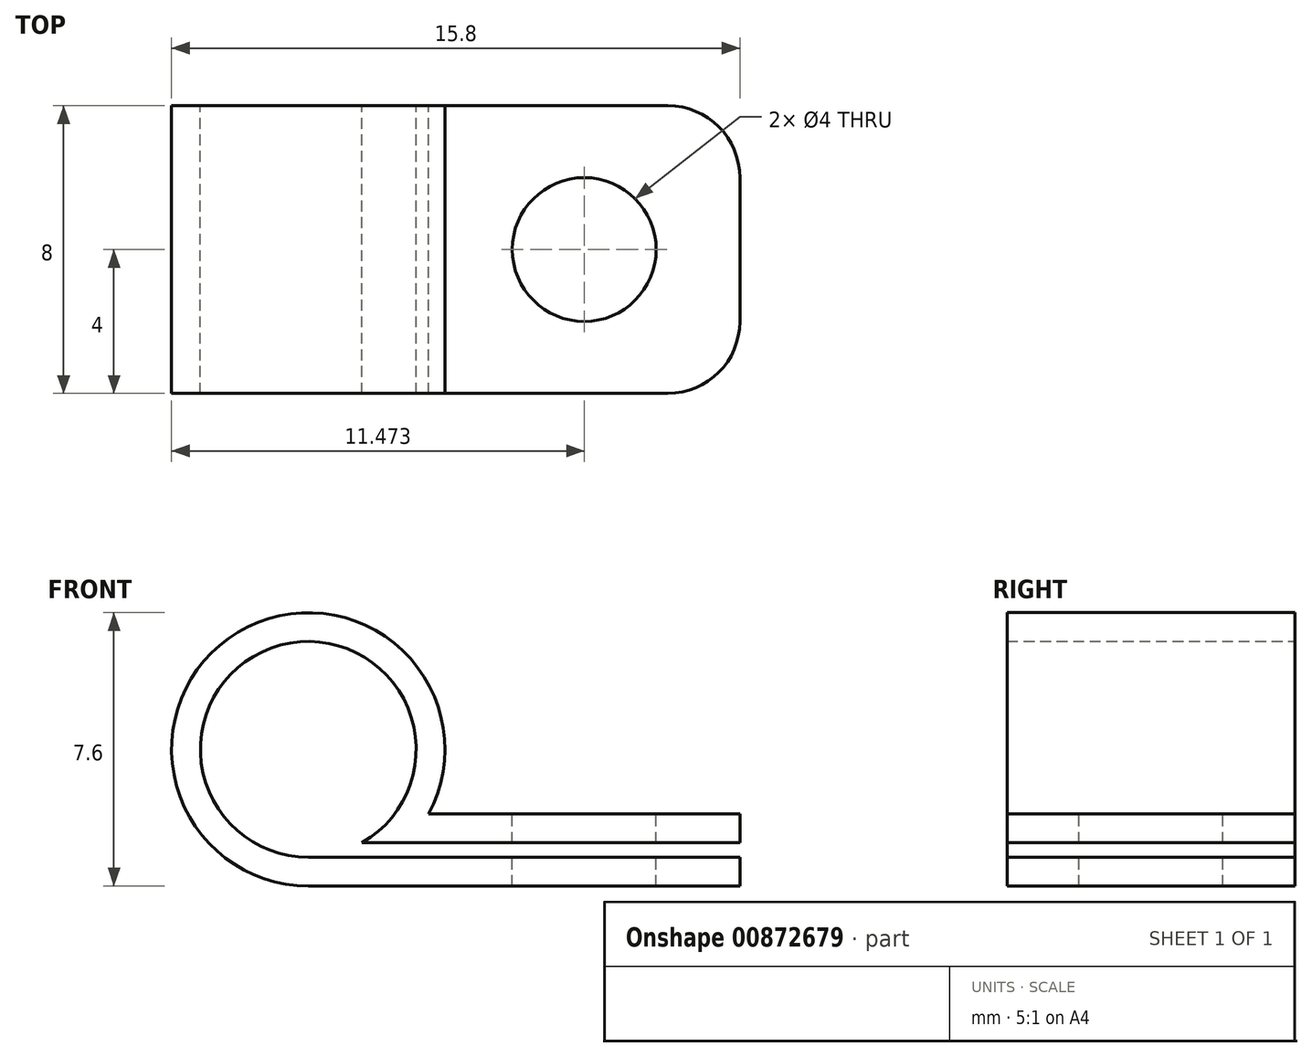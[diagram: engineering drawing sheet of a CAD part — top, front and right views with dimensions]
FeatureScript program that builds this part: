
annotation { "Feature Type Name" : "Feature", "Feature Type Description" : "" }
export const myFeature = defineFeature(function(context is Context, id is Id, definition is map)
    precondition{}
    {
        {
            var Q0;
            Q0=qCreatedBy(makeId("Front.planeOp"),FACE);
            var sketch = newSketch(context, id + "F0", { "sketchPlane" : qUnion([Q0])});
            skCircle(sketch, "E0", {"center": v(0, 0) * mm, "radius": 3 * mm});
            skCircle(sketch, "E1", {"center": v(0, 0) * mm, "radius": 3.8 * mm});
            skLineSegment(sketch, "E2.bottom", {"start": v(0, -3.8) * mm, "end": v(12, -3.8) * mm});
            skLineSegment(sketch, "E2.top", {"start": v(0, -3) * mm, "end": v(12, -3) * mm});
            skLineSegment(sketch, "E2.left", {"start": v(0, -3.8) * mm, "end": v(0, -3) * mm});
            skLineSegment(sketch, "E2.right", {"start": v(12, -3.8) * mm, "end": v(12, -3) * mm});
            skLineSegment(sketch, "E3", {"start": v(12, -3) * mm, "end": v(12, -2.6) * mm});
            skLineSegment(sketch, "E4.bottom", {"start": v(12, -2.6) * mm, "end": v(1.37, -2.6) * mm});
            skLineSegment(sketch, "E4.top", {"start": v(12, -1.8) * mm, "end": v(1.37, -1.8) * mm});
            skLineSegment(sketch, "E4.left", {"start": v(12, -2.6) * mm, "end": v(12, -1.8) * mm});
            skLineSegment(sketch, "E4.right", {"start": v(1.37, -2.6) * mm, "end": v(1.37, -1.8) * mm});
            skSolve(sketch);
        }
        {
            var Q0;
            {var subQ0=sQuery(id+"F0.wireOp",EDGE,"E2.left");Q0=makeQuery(id+"F0.imprint","IMPRINT",FACE,{"disambiguationData":[TD([[makeQuery(id+"F0.imprint","IMPRINT",EDGE,{"derivedFrom":subQ0}),1.0]])]});}
            var Q1;
            {var subQ0=sQuery(id+"F0.wireOp",EDGE,"l8cNaRmP-a3Ar-Ibxh-vkPG-nLSyhId6ISBD.bottom");var subQ1=sQuery(id+"F0.wireOp",EDGE,"E0");var subQ2=makeQuery(id+"F0.imprint","INTERSECT",VERTEX,{"derivedFrom":[subQ1,subQ0]});Q1=makeQuery(id+"F0.imprint","IMPRINT",FACE,{"disambiguationData":[TD([[makeQuery(id+"F0.imprint","IMPRINT",EDGE,{"disambiguationData":[TD([[subQ2,-1.0]])],"derivedFrom":subQ1}),-1.0]])]});}
            var Q2;
            {var subQ5=sQuery(id+"F0.wireOp",EDGE,"l8cNaRmP-a3Ar-Ibxh-vkPG-nLSyhId6ISBD.left");Q2=makeQuery(id+"F0.imprint","IMPRINT",FACE,{"disambiguationData":[TD([[makeQuery(id+"F0.imprint","IMPRINT",EDGE,{"derivedFrom":subQ5}),1.0]])]});}
            var Q3;
            {var subQ0=sQuery(id+"F0.wireOp",EDGE,"E2.bottom");Q3=makeQuery(id+"F0.imprint","IMPRINT",FACE,{"disambiguationData":[TD([[makeQuery(id+"F0.imprint","IMPRINT",EDGE,{"derivedFrom":subQ0}),1.0]])]});}
            var Q4;
            {var subQ0=sQuery(id+"F0.wireOp",EDGE,"E2.left");Q4=makeQuery(id+"F0.imprint","IMPRINT",FACE,{"disambiguationData":[TD([[makeQuery(id+"F0.imprint","IMPRINT",EDGE,{"derivedFrom":subQ0}),-1.0]])]});}
            var Q5;
            {var subQ0=sQuery(id+"F0.wireOp",EDGE,"E4.right");var subQ7=sQuery(id+"F0.wireOp",EDGE,"E0");var subQ9=makeQuery(id+"F0.imprint","INTERSECT",VERTEX,{"derivedFrom":[subQ7,subQ0]});Q5=makeQuery(id+"F0.imprint","IMPRINT",FACE,{"disambiguationData":[TD([[makeQuery(id+"F0.imprint","IMPRINT",EDGE,{"disambiguationData":[TD([[subQ9,-1.0]])],"derivedFrom":subQ7}),-1.0]])]});}
            var Q6;
            {var subQ5=sQuery(id+"F0.wireOp",EDGE,"E4.left");Q6=makeQuery(id+"F0.imprint","IMPRINT",FACE,{"disambiguationData":[TD([[makeQuery(id+"F0.imprint","IMPRINT",EDGE,{"derivedFrom":subQ5}),1.0]])]});}
            extrude(context, id + "F1", {"entities" : qUnion([Q0, Q1, Q2, Q3, Q4, Q5, Q6]), "depth" : 8 * mm, "offsetDistance" : 25 * mm});
        }
        {
            var Q0;
            Q0=makeQuery(id+"F1.opExtrude","SWEPT_FACE",FACE,{"disambiguationData":[OSD([sQuery(id+"F0.wireOp",EDGE,"E4.top")])]});
            var sketch = newSketch(context, id + "F2", { "sketchPlane" : qUnion([Q0])});
            skLineSegment(sketch, "E5", {"start": v(12, -4) * mm, "end": v(3.3, -4) * mm, "construction": true});
            skLineSegment(sketch, "E6", {"start": v(7.67, 0) * mm, "end": v(7.67, -8) * mm, "construction": true});
            skCircle(sketch, "E7", {"center": v(7.67, -4) * mm, "radius": 2 * mm});
            skSolve(sketch);
        }
        {
            var Q0;
            Q0=makeQuery(id+"F2.imprint","IMPRINT",FACE,{"disambiguationData":[TD([[makeQuery(id+"F2.imprint","IMPRINT",EDGE,{"derivedFrom":sQuery(id+"F2.wireOp",EDGE,"E7")}),1.0]])]});
            extrude(context, id + "F3", {"entities" : qUnion([Q0]), "operationType" : NewBodyOperationType.REMOVE, "oppositeDirection" : true, "depth" : 25 * mm, "offsetDistance" : 25 * mm});
        }
        {
            var Q0;
            Q0=makeQuery(id+"F1.opExtrude","CAP_EDGE",EDGE,{"disambiguationData":[OSD([sQuery(id+"F0.wireOp",EDGE,"E4.left")])],"isStart":false});
            var Q1;
            Q1=makeQuery(id+"F1.opExtrude","CAP_EDGE",EDGE,{"disambiguationData":[OSD([sQuery(id+"F0.wireOp",EDGE,"E2.right")])],"isStart":false});
            var Q2;
            Q2=makeQuery(id+"F1.opExtrude","CAP_EDGE",EDGE,{"disambiguationData":[OSD([sQuery(id+"F0.wireOp",EDGE,"E2.right")])],"isStart":true});
            var Q3;
            Q3=makeQuery(id+"F1.opExtrude","CAP_EDGE",EDGE,{"disambiguationData":[OSD([sQuery(id+"F0.wireOp",EDGE,"E4.left")])],"isStart":true});
            fillet(context, id + "F4", {"entities" : qUnion([Q0, Q1, Q2, Q3]), "radius" : 2 * mm, "tangentPropagation" : true, "allowEdgeOverflow" : false});
        }
    });
